FCSTD DOCUMENT  (FreeCAD 0.19.4R1_voidlinux)
Label: asm_back_shell
License: All rights reserved
LicenseURL: http://en.wikipedia.org/wiki/All_rights_reserved
objects: App::Link×6, App::DocumentObjectGroup×3, PartDesign::CoordinateSystem×1, App::FeaturePython×1, App::Part×1
note: 1 computed .brp shape members not serialized (recipe doc carries the construction recipe); baked Part::Feature solids carry a one-line shape summary decoded from their .brp
EXTERNAL_REF file=shell_back.FCStd obj=Part
EXTERNAL_REF file=asm_battery_container.FCStd obj=LCS_Origin
EXTERNAL_REF file=asm_battery_container.FCStd obj=Model
EXTERNAL_REF file=asm_wheel.FCStd obj=LCS_Origin
EXTERNAL_REF file=shell_back.FCStd obj=LCS_wheel_rest
EXTERNAL_REF file=asm_wheel.FCStd obj=Model
EXTERNAL_REF file=clock_inner.FCStd obj=LCS_1
EXTERNAL_REF file=clock_inner.FCStd obj=Part
EXTERNAL_REF file=alarm_button.FCStd obj=LCS_bottom_edge
EXTERNAL_REF file=shell_back.FCStd obj=LCS_alarm_button_edge
EXTERNAL_REF file=alarm_button.FCStd obj=Part
EXTERNAL_REF file=asm_back_lid.FCStd obj=LCS_Origin
EXTERNAL_REF file=asm_back_lid.FCStd obj=Model

FEATURE [App::DocumentObjectGroup] Parts
FEATURE [PartDesign::CoordinateSystem] LCS_Origin
  AttacherType = Attacher::AttachEngine3D
  MapMode = 2
  Support = -> [X_Axis]
FEATURE [App::DocumentObjectGroup] Constraints
FEATURE [App::FeaturePython] Variables  # WARN: FeaturePython — macro-defined, semantics opaque (R4)
  Type = App::PropertyContainer
FEATURE [App::DocumentObjectGroup] Configurations
FEATURE [App::Link] battery_body_part
  LinkedObject = -> <external shell_back.FCStd>#Part
FEATURE [App::Link] asm_battery_container
  AttachedBy = #LCS_Origin
  AttachedTo = Parent Assembly#LCS_Origin
  AttachmentOffset = pos=(0,3.6,-4) rot=(0,0,1;0rad)
  LinkPlacement = pos=(0,3.6,-4) rot=(0,0,1;0rad)
  LinkedObject = -> <external asm_battery_container.FCStd>#Model
  Placement = pos=(0,3.6,-4) rot=(0,0,1;0rad)
  SolverId = Asm4EE
  expr: Placement = LCS_Origin.Placement * AttachmentOffset * asm_battery_container#LCS_Origin.Placement ^ -1
FEATURE [App::Link] asm_wheel
  AttachedBy = #LCS_Origin
  AttachedTo = battery_body_part#LCS_wheel_rest
  AttachmentOffset = pos=(0,0,2) rot=(0,0,1;0rad)
  LinkPlacement = pos=(7,38,18) rot=(0,0,1;1.5708rad)
  LinkedObject = -> <external asm_wheel.FCStd>#Model
  Placement = pos=(7,38,18) rot=(0,0,1;1.5708rad)
  SolverId = Asm4EE
  expr: Placement = battery_body_part.Placement * shell_back#LCS_wheel_rest.Placement * AttachmentOffset * asm_wheel#LCS_Origin.Placement ^ -1
FEATURE [App::Link] clock_inner
  AttachedBy = #LCS_1
  AttachedTo = Parent Assembly#LCS_Origin
  AttachmentOffset = pos=(0,39.6,11) rot=(0,0,1;1.5708rad)
  LinkPlacement = pos=(-3e-16,22.1,-4) rot=(0,0,1;0rad)
  LinkedObject = -> <external clock_inner.FCStd>#Part
  Placement = pos=(-3e-16,22.1,-4) rot=(0,0,1;0rad)
  SolverId = Asm4EE
  expr: Placement = LCS_Origin.Placement * AttachmentOffset * clock_inner#LCS_1.Placement ^ -1
FEATURE [App::Link] alarm_button
  AttachedBy = #LCS_bottom_edge
  AttachedTo = battery_body_part#LCS_alarm_button_edge
  AttachmentOffset = pos=(0,0,0) rot=(0.707107,0.707107,0;3.14159rad)
  LinkPlacement = pos=(5.8e-15,63.5,-3.5) rot=(0,0.707107,0.707107;3.14159rad)
  LinkedObject = -> <external alarm_button.FCStd>#Part
  Placement = pos=(5.8e-15,63.5,-3.5) rot=(0,0.707107,0.707107;3.14159rad)
  SolverId = Asm4EE
  expr: Placement = battery_body_part.Placement * shell_back#LCS_alarm_button_edge.Placement * AttachmentOffset * alarm_button#LCS_bottom_edge.Placement ^ -1
FEATURE [App::Link] back_lid_model
  AttachedBy = #LCS_Origin
  AttachedTo = Parent Assembly#LCS_Origin
  AttachmentOffset = pos=(0,0,18) rot=(0,1,0;3.14159rad)
  LinkPlacement = pos=(0,0,18) rot=(0,1,0;3.14159rad)
  LinkedObject = -> <external asm_back_lid.FCStd>#Model
  Placement = pos=(0,0,18) rot=(0,1,0;3.14159rad)
  SolverId = Asm4EE
  expr: Placement = LCS_Origin.Placement * AttachmentOffset * asm_back_lid#LCS_Origin.Placement ^ -1
FEATURE [App::Part] Model
  AssemblyType = Part::Link
  Group = -> [LCS_Origin,Constraints,Variables,Configurations,battery_body_part,asm_battery_container,asm_wheel,clock_inner,alarm_button,back_lid_model]
  Origin = -> Origin
  Type = Assembly

RESOLVED EXTERNAL PARTS (link-assembly join: the EXTERNAL_REF files above that resolve inside this repo's crawl, each included once):
---- part alarm_button.FCStd = doc fcstd_2c8dfa710c5f ----
FCSTD DOCUMENT  (FreeCAD 0.19.4R1_voidlinux)
Label: alarm_button
License: All rights reserved
LicenseURL: http://en.wikipedia.org/wiki/All_rights_reserved
objects: Sketcher::SketchObject×3, PartDesign::Pad×2, PartDesign::Fillet×2, PartDesign::Pocket×1, PartDesign::LinearPattern×1, PartDesign::Point×1, PartDesign::Body×1, PartDesign::CoordinateSystem×1, App::Part×1
note: 17 computed .brp shape members not serialized (recipe doc carries the construction recipe); baked Part::Feature solids carry a one-line shape summary decoded from their .brp
EXTERNAL_REF file=master_animator.FCStd obj=Variables

FEATURE [Sketcher::SketchObject] Sketch
  FullyConstrained = true
  MapMode = 5
  Placement = pos=(0,0,0) rot=(0.57735,0.57735,0.57735;2.0944rad)
  Support = -> [YZ_Plane001]
  sketch-geometry (9):
    g0: LineSegment StartX=0 StartY=0 StartZ=0 EndX=21.5 EndY=0 EndZ=0
    g1: LineSegment StartX=21.5 StartY=0 StartZ=0 EndX=21.5 EndY=-9.7 EndZ=0
    g2: LineSegment StartX=21.5 StartY=-9.7 StartZ=0 EndX=22.3 EndY=-9.7 EndZ=0
    g3: ArcOfCircle CenterX=22.3 CenterY=-10.6 CenterZ=0 NormalX=0 NormalY=0 NormalZ=1 AngleXU=0 Radius=0.9 StartAngle=4.71239 EndAngle=7.85398
    g4: LineSegment StartX=22.3 StartY=-9.7 StartZ=0 EndX=22.3 EndY=-11.5 EndZ=0
    g5: LineSegment StartX=22.3 StartY=-11.5 StartZ=0 EndX=19.5 EndY=-11.5 EndZ=0
    g6: LineSegment StartX=19.5 StartY=-11.5 StartZ=0 EndX=19.5 EndY=-4.5 EndZ=0
    g7: LineSegment StartX=19.5 StartY=-4.5 StartZ=0 EndX=0 EndY=-4.5 EndZ=0
    g8: LineSegment StartX=0 StartY=-4.5 StartZ=0 EndX=0 EndY=0 EndZ=0
  constraints (25):
    c: Coincident(g0,g-1)
    c: Coincident(g1,g0)
    c: Vertical(g1)
    c: Coincident(g2,g1)
    c: Horizontal(g2)
    c: Tangent(g3,g2) = 1.5708
    c: Coincident(g4,g2)
    c: Coincident(g4,g3)
    c: Vertical(g4)
    c: Coincident(g5,g3)
    c: Horizontal(g5)
    c: Coincident(g6,g5)
    c: Vertical(g6)
    c: Coincident(g7,g6)
    c: PointOnObject(g7,g-2)
    c: Horizontal(g7)
    c: Coincident(g8,g7)
    c: Coincident(g8,g0)
    c: Distance(g4) = 1.8
    c: DistanceY(g3,g0) = 11.5
    c: Distance(g8) = 4.5
    c: Horizontal(g0)
    c: Distance(g0) = 21.5
    c: DistanceX(g6,g0) = 2
    c: DistanceX(g1,g3) = 0.8
FEATURE [PartDesign::Pad] Pad
  Direction = (1,1,1)
  Length = 19.5
  Length2 = 100
  Midplane = true
  Placement = pos=(0,0,0) rot=(0.57735,0.57735,0.57735;2.0944rad)
  Profile = -> Sketch
  Type = 0
FEATURE [PartDesign::Fillet] Fillet
  Base = -> Pad [Edge24,Edge23]
  BaseFeature = -> Pad
  Placement = pos=(0,0,0) rot=(0.57735,0.57735,0.57735;2.0944rad)
  Radius = 2
  SupportTransform = false
FEATURE [Sketcher::SketchObject] Sketch001
  ExternalGeometry = -> [Fillet]
  FullyConstrained = true
  MapMode = 5
  Placement = pos=(0,0,0) rot=(0,0,-1;1.5708rad)
  Support = -> [Fillet]
  sketch-geometry (6):
    g0: ArcOfCircle CenterX=-2 CenterY=7.75 CenterZ=0 NormalX=0 NormalY=0 NormalZ=1 AngleXU=0 Radius=1 StartAngle=6.28318 EndAngle=7.85398
    g1: ArcOfCircle CenterX=-2 CenterY=-7.75 CenterZ=0 NormalX=0 NormalY=0 NormalZ=1 AngleXU=0 Radius=0.999961 StartAngle=4.71239 EndAngle=6.28318
    g2: LineSegment StartX=-19.25 StartY=8.75 StartZ=0 EndX=-19.25 EndY=-8.74996 EndZ=0
    g3: LineSegment StartX=-19.25 StartY=-8.74996 StartZ=0 EndX=-2 EndY=-8.74996 EndZ=0
    g4: LineSegment StartX=-19.25 StartY=8.75 StartZ=0 EndX=-2 EndY=8.75 EndZ=0
    g5: LineSegment StartX=-1 StartY=7.75 StartZ=0 EndX=-1.00004 EndY=-7.75 EndZ=0
  constraints (14):
    c: Vertical(g2)
    c: Coincident(g3,g2)
    c: Horizontal(g3)
    c: Coincident(g4,g2)
    c: Horizontal(g4)
    c: Tangent(g4,g0) = 1.5708
    c: Tangent(g1,g3) = -1.5708
    c: Tangent(g5,g1) = 1.5708
    c: Tangent(g5,g0) = 1.5708
    c: Symmetric(g0,g1,g-1)
    c: DistanceY(g2,g-5) = 1
    c: DistanceX(g-5,g2) = 2.25
    c: DistanceX(g0,g-3) = 1
    c: Coincident(g0,g-3)
FEATURE [PartDesign::Pocket] Pocket
  BaseFeature = -> Fillet
  Length = 0.5
  Length2 = 100
  Placement = pos=(0,0,0) rot=(0.57735,0.57735,0.57735;2.0944rad)
  Profile = -> Sketch001
  Type = 0
FEATURE [Sketcher::SketchObject] Sketch002
  ExternalGeometry = -> [Pocket]
  FullyConstrained = true
  MapMode = 5
  Placement = pos=(-8.74996,1.9e-15,-5.3e-15) rot=(0.57735,0.57735,0.57735;2.0944rad)
  Support = -> [Pocket]
  expr: Constraints[6] = 17.5 / 17
  sketch-geometry (5):
    g0: LineSegment StartX=18.2206 StartY=-0.05 StartZ=0 EndX=18.2206 EndY=-0.5 EndZ=0
    g1: LineSegment StartX=18.2206 StartY=-0.05 StartZ=0 EndX=18.7353 EndY=-0.4 EndZ=0
    g2: LineSegment StartX=18.7353 StartY=-0.4 StartZ=0 EndX=19.25 EndY=-0.05 EndZ=0
    g3: LineSegment StartX=19.25 StartY=-0.5 StartZ=0 EndX=19.25 EndY=-0.05 EndZ=0
    g4: LineSegment StartX=19.25 StartY=-0.5 StartZ=0 EndX=18.2206 EndY=-0.5 EndZ=0
  constraints (14):
    c: PointOnObject(g0,g-3)
    c: Vertical(g0)
    c: Coincident(g1,g0)
    c: Coincident(g2,g1)
    c: Equal(g1,g2)
    c: DistanceY(g0,g1) = 0.1
    c: DistanceX(g0,g2) = 1.02941
    c: Coincident(g3,g2)
    c: Vertical(g3)
    c: DistanceY(g0,g2) = 0
    c: Coincident(g4,g3)
    c: Coincident(g4,g0)
    c: Coincident(g3,g-3)
    c: DistanceY(g2,g-4) = 0.05
FEATURE [PartDesign::Pad] Pad001
  BaseFeature = -> Pocket
  Direction = (1,1,1)
  Length = 10
  Length2 = 100
  Placement = pos=(0,0,0) rot=(0.57735,0.57735,0.57735;2.0944rad)
  Profile = -> Sketch002
  Type = 2
FEATURE [PartDesign::LinearPattern] LinearPattern
  BaseFeature = -> Pad001
  Direction = -> Y_Axis001
  Length = 17.5
  Occurrences = 18
  Originals = -> [Pad001]
  Placement = pos=(0,0,0) rot=(0.57735,0.57735,0.57735;2.0944rad)
  Reversed = true
FEATURE [PartDesign::Fillet] Fillet001
  Base = -> LinearPattern [Edge6]
  BaseFeature = -> LinearPattern
  Placement = pos=(0,0,0) rot=(0.57735,0.57735,0.57735;2.0944rad)
  Radius = 1.5
  SupportTransform = false
FEATURE [PartDesign::Point] DatumPoint
  AttacherType = Attacher::AttachEnginePoint
  MapMode = 37
  Placement = pos=(8.9e-15,19.5,-11.5) rot=(0,0,1;0rad)
  Support = -> [Fillet001]
FEATURE [PartDesign::Body] Body
  Group = -> [Sketch,Pad,Fillet,Sketch001,Pocket,Sketch002,Pad001,LinearPattern,Fillet001,DatumPoint]
  Origin = -> Origin001
  Tip = -> Fillet001
FEATURE [PartDesign::CoordinateSystem] LCS_bottom_edge
  AttacherType = Attacher::AttachEngine3D
  MapMode = 1
  Placement = pos=(8.9e-15,19.5,-11.5) rot=(0.57735,0.57735,0.57735;2.0944rad)
  Support = -> [DatumPoint]
  expr: .AttachmentOffset.Base.z = -master_animator#Variables.explode * 2
FEATURE [App::Part] Part  label="alarm_button"
  Group = -> [Body,LCS_bottom_edge]
  Origin = -> Origin
---- part asm_back_lid.FCStd = doc fcstd_fb15be1f9ad7 ----
FCSTD DOCUMENT  (FreeCAD 0.19.4R1_voidlinux)
Label: asm_back_lid
License: All rights reserved
LicenseURL: http://en.wikipedia.org/wiki/All_rights_reserved
objects: App::DocumentObjectGroup×3, App::Link×2, PartDesign::CoordinateSystem×1, App::FeaturePython×1, App::Part×1
note: 1 computed .brp shape members not serialized (recipe doc carries the construction recipe); baked Part::Feature solids carry a one-line shape summary decoded from their .brp
EXTERNAL_REF file=master_animator.FCStd obj=Variables
EXTERNAL_REF file=back_lid.FCStd obj=Part
EXTERNAL_REF file=back_lid.FCStd obj=LCS_foam_attach
EXTERNAL_REF file=back_lid_foam.FCStd obj=foam_back_center
EXTERNAL_REF file=back_lid_foam.FCStd obj=Part

FEATURE [App::DocumentObjectGroup] Parts
FEATURE [PartDesign::CoordinateSystem] LCS_Origin
  AttacherType = Attacher::AttachEngine3D
  MapMode = 2
  Support = -> [X_Axis]
  expr: .AttachmentOffset.Base.y = master_animator#Variables.explode * 3
FEATURE [App::DocumentObjectGroup] Constraints
FEATURE [App::FeaturePython] Variables  # WARN: FeaturePython — macro-defined, semantics opaque (R4)
  Type = App::PropertyContainer
FEATURE [App::DocumentObjectGroup] Configurations
FEATURE [App::Link] back_lid
  LinkedObject = -> <external back_lid.FCStd>#Part
FEATURE [App::Link] back_lid_foam
  AssemblyType = Part::Link
  AttachedBy = #foam_back_center
  AttachedTo = back_lid#LCS_foam_attach
  LinkPlacement = pos=(1e-16,7.5,2.1) rot=(0,0,1;0rad)
  LinkedObject = -> <external back_lid_foam.FCStd>#Part
  Placement = pos=(1e-16,7.5,2.1) rot=(0,0,1;0rad)
  SolverId = Asm4EE
  expr: Placement = back_lid.Placement * back_lid#LCS_foam_attach.Placement * AttachmentOffset * back_lid_foam#foam_back_center.Placement ^ -1
FEATURE [App::Part] Model  label="back_lid_model"
  Group = -> [LCS_Origin,Constraints,Variables,Configurations,back_lid,back_lid_foam]
  Origin = -> Origin
  Type = Assembly
---- part asm_battery_container.FCStd = doc fcstd_e6c359b65b27 ----
FCSTD DOCUMENT  (FreeCAD 0.19.4R1_voidlinux)
Label: asm_battery_container
License: All rights reserved
LicenseURL: http://en.wikipedia.org/wiki/All_rights_reserved
objects: App::Link×4, App::DocumentObjectGroup×3, PartDesign::CoordinateSystem×1, App::FeaturePython×1, App::Part×1
note: 1 computed .brp shape members not serialized (recipe doc carries the construction recipe); baked Part::Feature solids carry a one-line shape summary decoded from their .brp
EXTERNAL_REF file=master_animator.FCStd obj=Variables
EXTERNAL_REF file=battery_container.FCStd obj=Part
EXTERNAL_REF file=battery_contact_minus.FCStd obj=LCS_tangent_to_container
EXTERNAL_REF file=battery_container.FCStd obj=LCS_minus_face
EXTERNAL_REF file=battery_contact_minus.FCStd obj=Part
EXTERNAL_REF file=battery_contact_plus.FCStd obj=LCS_bottom_face
EXTERNAL_REF file=battery_container.FCStd obj=LCS_plus_bottom
EXTERNAL_REF file=battery_contact_plus.FCStd obj=Part
EXTERNAL_REF file=battery_aa.FCStd obj=LCS_plus_center
EXTERNAL_REF file=battery_contact_plus.FCStd obj=LCS_plus_center
EXTERNAL_REF file=battery_aa.FCStd obj=Part

FEATURE [App::DocumentObjectGroup] Parts
FEATURE [PartDesign::CoordinateSystem] LCS_Origin
  AttacherType = Attacher::AttachEngine3D
  MapMode = 2
  Support = -> [X_Axis]
  expr: .AttachmentOffset.Base.z = -master_animator#Variables.explode * 4
FEATURE [App::DocumentObjectGroup] Constraints
FEATURE [App::FeaturePython] Variables  # WARN: FeaturePython — macro-defined, semantics opaque (R4)
  Type = App::PropertyContainer
FEATURE [App::DocumentObjectGroup] Configurations
FEATURE [App::Link] battery_container
  LinkedObject = -> <external battery_container.FCStd>#Part
FEATURE [App::Link] battery_contact_minus
  AttachedBy = #LCS_tangent_to_container
  AttachedTo = battery_container#LCS_minus_face
  AttachmentOffset = pos=(4,-0.5,0) rot=(0,0,1;0rad)
  LinkPlacement = pos=(-26.5,17.3333,3.83333) rot=(0,0,1;0rad)
  LinkedObject = -> <external battery_contact_minus.FCStd>#Part
  Placement = pos=(-26.5,17.3333,3.83333) rot=(0,0,1;0rad)
  SolverId = Asm4EE
  expr: Placement = battery_container.Placement * battery_container#LCS_minus_face.Placement * AttachmentOffset * battery_contact_minus#LCS_tangent_to_container.Placement ^ -1
FEATURE [App::Link] battery_contact_plus
  AttachedBy = #LCS_bottom_face
  AttachedTo = battery_container#LCS_minus_face
  AttachmentOffset = pos=(0.3,4,0) rot=(0,0,1;0rad)
  LinkPlacement = pos=(26.4,19.5,4.33563) rot=(0,0,1;0rad)
  LinkedObject = -> <external battery_contact_plus.FCStd>#Part
  Placement = pos=(26.4,19.5,4.33563) rot=(0,0,1;0rad)
  SolverId = Asm4EE
  expr: Placement = battery_container.Placement * battery_container#LCS_plus_bottom.Placement * AttachmentOffset * battery_contact_plus#LCS_bottom_face.Placement ^ -1
FEATURE [App::Link] battery_aa
  AssemblyType = Part::Link
  AttachedBy = #LCS_plus_center
  AttachedTo = battery_contact_plus#LCS_plus_center
  LinkPlacement = pos=(-23.9,8.5,7.73563) rot=(0.57735,-0.57735,0.57735;4.18879rad)
  LinkedObject = -> <external battery_aa.FCStd>#Part
  Placement = pos=(-23.9,8.5,7.73563) rot=(0.57735,-0.57735,0.57735;4.18879rad)
  SolverId = Asm4EE
  expr: Placement = battery_contact_plus.Placement * battery_contact_plus#LCS_plus_center.Placement * AttachmentOffset * battery_aa#LCS_plus_center.Placement ^ -1
FEATURE [App::Part] Model
  Group = -> [LCS_Origin,Constraints,Variables,Configurations,battery_container,battery_contact_minus,battery_contact_plus,battery_aa]
  Origin = -> Origin
  Type = Assembly
---- part asm_wheel.FCStd = doc fcstd_0f8f7559fc01 ----
FCSTD DOCUMENT  (FreeCAD 0.19.4R1_voidlinux)
Label: asm_wheel
License: All rights reserved
LicenseURL: http://en.wikipedia.org/wiki/All_rights_reserved
objects: App::DocumentObjectGroup×3, App::Link×2, PartDesign::CoordinateSystem×1, App::FeaturePython×1, App::Part×1
note: 1 computed .brp shape members not serialized (recipe doc carries the construction recipe); baked Part::Feature solids carry a one-line shape summary decoded from their .brp
EXTERNAL_REF file=master_animator.FCStd obj=Variables
EXTERNAL_REF file=wheel.FCStd obj=Part
EXTERNAL_REF file=wheel.FCStd obj=LCS_axis_rest
EXTERNAL_REF file=wheel_axis.FCStd obj=LCS_axis_rest
EXTERNAL_REF file=wheel_axis.FCStd obj=Part

FEATURE [App::DocumentObjectGroup] Parts
FEATURE [PartDesign::CoordinateSystem] LCS_Origin
  AttacherType = Attacher::AttachEngine3D
  MapMode = 2
  Support = -> [X_Axis]
  expr: .AttachmentOffset.Base.z = -master_animator#Variables.explode * 4
FEATURE [App::DocumentObjectGroup] Constraints
FEATURE [App::FeaturePython] Variables  # WARN: FeaturePython — macro-defined, semantics opaque (R4)
  Type = App::PropertyContainer
FEATURE [App::DocumentObjectGroup] Configurations
FEATURE [App::Link] wheel
  LinkedObject = -> <external wheel.FCStd>#Part
FEATURE [App::Link] wheel_axis
  AttachedBy = #LCS_axis_rest
  AttachedTo = wheel#LCS_axis_rest
  LinkPlacement = pos=(-1.1e-15,8e-16,-0.5) rot=(0,0,1;0rad)
  LinkedObject = -> <external wheel_axis.FCStd>#Part
  Placement = pos=(-1.1e-15,8e-16,-0.5) rot=(0,0,1;0rad)
  SolverId = Asm4EE
  expr: Placement = wheel.Placement * wheel#LCS_axis_rest.Placement * AttachmentOffset * wheel_axis#LCS_axis_rest.Placement ^ -1
FEATURE [App::Part] Model
  Group = -> [LCS_Origin,Constraints,Variables,Configurations,wheel,wheel_axis]
  Origin = -> Origin
  Type = Assembly
---- part clock_inner.FCStd = doc fcstd_8776be697fff ----
FCSTD DOCUMENT  (FreeCAD 0.19.4R1_voidlinux)
Label: clock_inner
License: All rights reserved
LicenseURL: http://en.wikipedia.org/wiki/All_rights_reserved
objects: Sketcher::SketchObject×1, PartDesign::Pad×1, PartDesign::Body×1, Part::Fillet×1, PartDesign::CoordinateSystem×1, App::Part×1
note: 6 computed .brp shape members not serialized (recipe doc carries the construction recipe); baked Part::Feature solids carry a one-line shape summary decoded from their .brp
EXTERNAL_REF file=master_animator.FCStd obj=Variables

FEATURE [Sketcher::SketchObject] Sketch
  FullyConstrained = true
  MapMode = 5
  Support = -> [XY_Plane001]
  sketch-geometry (4):
    g0: LineSegment StartX=-28 StartY=35 StartZ=0 EndX=28 EndY=35 EndZ=0
    g1: LineSegment StartX=28 StartY=35 StartZ=0 EndX=28 EndY=0 EndZ=0
    g2: LineSegment StartX=28 StartY=0 StartZ=0 EndX=-28 EndY=0 EndZ=0
    g3: LineSegment StartX=-28 StartY=0 StartZ=0 EndX=-28 EndY=35 EndZ=0
  constraints (11):
    c: Coincident(g0,g1)
    c: Coincident(g1,g2)
    c: Coincident(g2,g3)
    c: Coincident(g3,g0)
    c: Horizontal(g0)
    c: Vertical(g1)
    c: Vertical(g3)
    c: Symmetric(g1,g2,g-2)
    c: Distance(g2) = 56
    c: Distance(g3) = 35
    c: PointOnObject(g2,g-1)
FEATURE [PartDesign::Pad] Pad
  Direction = (1,1,1)
  Length = 15
  Length2 = 100
  Profile = -> Sketch
  Type = 0
FEATURE [PartDesign::Body] Body
  Group = -> [Sketch,Pad]
  Origin = -> Origin001
  Tip = -> Pad
FEATURE [Part::Fillet] Fillet
  Base = -> Body
  Edges = 12 edges r=2: [Edge1,Edge2,Edge3,Edge4,Edge5,Edge6,Edge7,Edge8,Edge9,Edge10,Edge11,Edge12]
FEATURE [PartDesign::CoordinateSystem] LCS_1
  AttacherType = Attacher::AttachEngine3D
  MapMode = 45
  Placement = pos=(1e-15,17.5,15) rot=(0,0,1;1.5708rad)
  Support = -> [Fillet]
  expr: .AttachmentOffset.Base.z = master_animator#Variables.explode * 2
FEATURE [App::Part] Part  label="clock_inner"
  Group = -> [Body,Fillet,LCS_1]
  Origin = -> Origin
---- part shell_back.FCStd = doc fcstd_f4c27f3473d2 (69777 chars; too large to inline — full recipe in that document) ----
